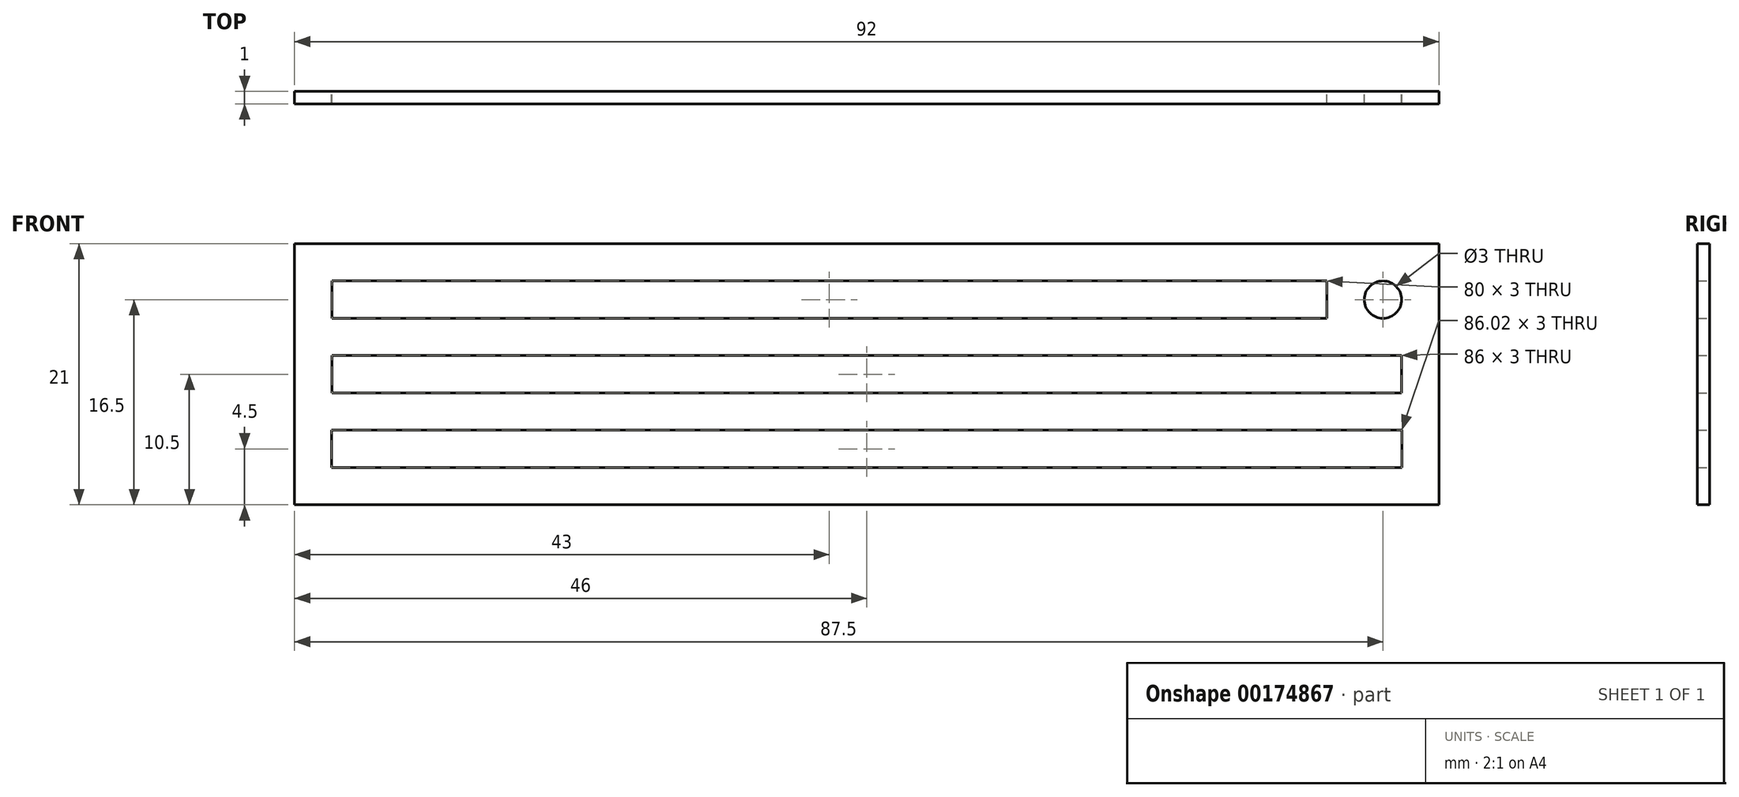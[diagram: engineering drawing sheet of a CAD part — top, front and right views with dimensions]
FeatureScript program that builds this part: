
annotation { "Feature Type Name" : "Feature", "Feature Type Description" : "" }
export const myFeature = defineFeature(function(context is Context, id is Id, definition is map)
    precondition{}
    {
        {
            var Q0;
            Q0=qCreatedBy(makeId("Front.planeOp"),FACE);
            var sketch = newSketch(context, id + "F0", { "sketchPlane" : qUnion([Q0])});
            skLineSegment(sketch, "E0.bottom", {"start": v(46, 10.5) * mm, "end": v(-46, 10.5) * mm});
            skLineSegment(sketch, "E0.top", {"start": v(46, -10.5) * mm, "end": v(-46, -10.5) * mm});
            skLineSegment(sketch, "E0.left", {"start": v(46, 10.5) * mm, "end": v(46, -10.5) * mm});
            skLineSegment(sketch, "E0.right", {"start": v(-46, 10.5) * mm, "end": v(-46, -10.5) * mm});
            skPoint(sketch, "E0.middle", {"position": v(0, 0) * mm});
            skLineSegment(sketch, "E1.bottom", {"start": v(43, 1.5) * mm, "end": v(-43, 1.5) * mm});
            skLineSegment(sketch, "E1.top", {"start": v(43, -1.5) * mm, "end": v(-43, -1.5) * mm});
            skLineSegment(sketch, "E1.left", {"start": v(43, 1.5) * mm, "end": v(43, -1.5) * mm});
            skLineSegment(sketch, "E1.right", {"start": v(-43, 1.5) * mm, "end": v(-43, -1.5) * mm});
            skLineSegment(sketch, "E2.bottom", {"start": v(43.01, -4.5) * mm, "end": v(-43.01, -4.5) * mm});
            skLineSegment(sketch, "E2.top", {"start": v(43.01, -7.5) * mm, "end": v(-43.01, -7.5) * mm});
            skLineSegment(sketch, "E2.left", {"start": v(43.01, -4.5) * mm, "end": v(43.01, -7.5) * mm});
            skLineSegment(sketch, "E2.right", {"start": v(-43.01, -4.5) * mm, "end": v(-43.01, -7.5) * mm});
            skPoint(sketch, "E2.middle", {"position": v(0, -6) * mm});
            skLineSegment(sketch, "E3.bottom", {"start": v(-43, 4.5) * mm, "end": v(37, 4.5) * mm});
            skLineSegment(sketch, "E3.top", {"start": v(-43, 7.5) * mm, "end": v(37, 7.5) * mm});
            skLineSegment(sketch, "E3.left", {"start": v(-43, 4.5) * mm, "end": v(-43, 7.5) * mm});
            skLineSegment(sketch, "E3.right", {"start": v(37, 4.5) * mm, "end": v(37, 7.5) * mm});
            skCircle(sketch, "E4", {"center": v(41.5, 6) * mm, "radius": 1.5 * mm});
            skSolve(sketch);
        }
        {
            var Q0;
            Q0 = qSketchRegion(id + "F0", true);
            extrude(context, id + "F1", {"entities" : qUnion([Q0]), "depth" : 1 * mm});
        }
    });
